# Revit family: CSWEU2LED
name_source: partatom
category: Lighting Fixtures
units: mm (PartAtom-declared; Revit-internal decimal feet)

## family parameters
Cut with Voids When Loaded = No
Host = Face
Light Source = No
OmniClass Number = 23.80.70.11.21
OmniClass Title = Emergency Lighting
Part Type = Normal
Room Calculation Point = No
Round Connector Dimension = Use Diameter
Shared = No

## types (1)
- CSWEU2LED
    Apparent Load = 2 VA
    Default Elevation = 48 "
    Description = Outdoor LED emergency light with fully gasketed polycarbonate shield
    Glass Shield = White Glass
    Is 120V = No
    Is 270V = Yes
    Lamp = LED life-cycle of more than 10 years
    Load Classification = Lighting
    Manufacturer = Compass Products
    Material = White
    Model = CSWEU2LED
    Mounting = Wall or Ceiling mount
    Power Factor = 1
    URL = https://www.currentlighting.com
    Voltage = 270 V
    Warranty = 2 year full unit warranty
    Watt = 2 W
    Wattage Comments = 1.15W per lamp

## geometry (parser evidence)
native form markers: Blend x27, Sweep x4
no freeform markers — native parametric forms only
